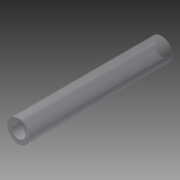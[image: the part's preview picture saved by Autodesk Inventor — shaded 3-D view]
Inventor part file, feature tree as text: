
AUTODESK INVENTOR PART (.ipt)
format: ipt  version: 2014 SP1 (Build 180222100, 222)  size: 75,776 bytes
history: native  units: in
note: dims shown in document units (in); Inventor stores cm internally (conversion verified against a paired STEP export)
features: extrude x1, sketch x1
ambient origin geometry x8: Origin, YZ Plane, XZ Plane, XY Plane, X Axis, Y Axis, Z Axis, Center Point
bodies: Solid1 (feature_tree)
feature tree (2):
  extrude  "Extrusion1"  Depth=4.0in
  sketch  "Sketch1"  dims[d0=0.375in d1=0.625in d2=4.0in d3=0.0in]
